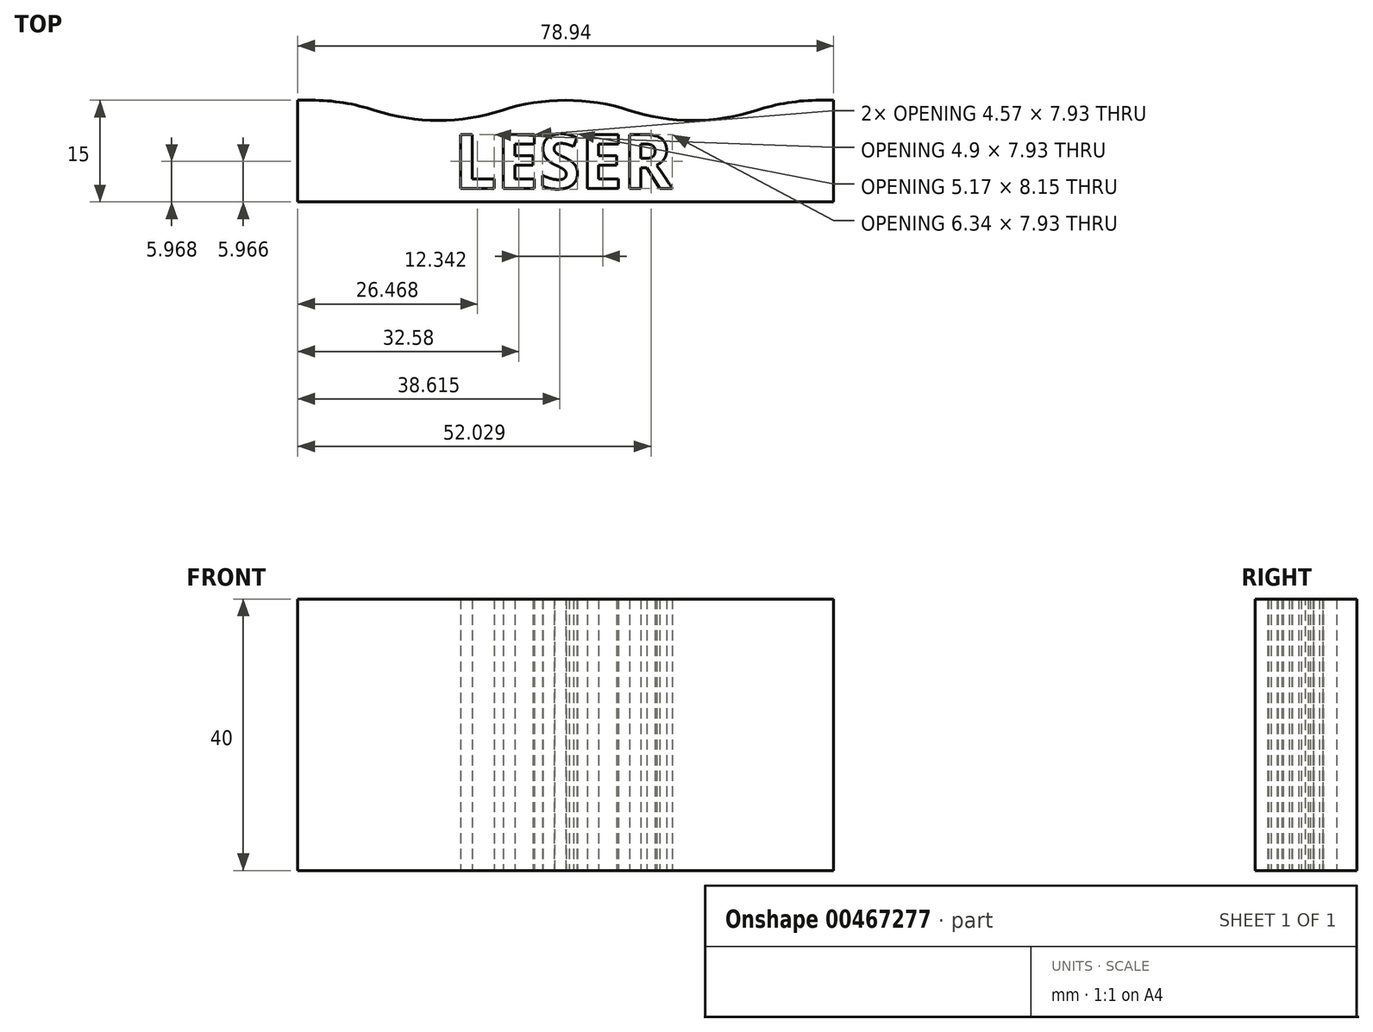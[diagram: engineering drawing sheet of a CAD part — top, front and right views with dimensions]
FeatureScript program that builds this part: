
annotation { "Feature Type Name" : "Feature", "Feature Type Description" : "" }
export const myFeature = defineFeature(function(context is Context, id is Id, definition is map)
    precondition{}
    {
        {
            var Q0;
            Q0=qCreatedBy(makeId("Top.planeOp"),FACE);
            var sketch = newSketch(context, id + "F0", { "sketchPlane" : qUnion([Q0])});
            skLineSegment(sketch, "E0", {"start": v(0, 0) * mm, "end": v(0, 15) * mm});
            skLineSegment(sketch, "E1", {"start": v(0, 15) * mm, "end": v(2, 15) * mm});
            skArc(sketch, "E2", {"start": v(2, 15) * mm, "mid": v(6.74, 14.62) * mm, "end": v(11.37, 13.5) * mm});
            skArc(sketch, "E3", {"start": v(11.37, 13.5) * mm, "mid": v(20.73, 12) * mm, "end": v(30.1, 13.5) * mm});
            skPoint(sketch, "E4.endSnap0", {"position": v(1, 15) * mm});
            skArc(sketch, "E5", {"start": v(30.1, 13.5) * mm, "mid": v(39.47, 15) * mm, "end": v(48.84, 13.5) * mm});
            skArc(sketch, "E6", {"start": v(48.84, 13.5) * mm, "mid": v(58.2, 12) * mm, "end": v(67.57, 13.5) * mm});
            skArc(sketch, "E7", {"start": v(67.57, 13.5) * mm, "mid": v(72.2, 14.62) * mm, "end": v(76.94, 15) * mm});
            skLineSegment(sketch, "E8", {"start": v(76.94, 15) * mm, "end": v(78.94, 15) * mm});
            skLineSegment(sketch, "E9", {"start": v(78.94, 15) * mm, "end": v(78.94, 0) * mm});
            skLineSegment(sketch, "E10", {"start": v(78.94, 0) * mm, "end": v(0, 0) * mm});
            skSolve(sketch);
        }
        {
            var Q0;
            Q0=makeQuery(id+"F0.imprint","IMPRINT",FACE,{"disambiguationData":[TD([[makeQuery(id+"F0.imprint","IMPRINT",EDGE,{"derivedFrom":sQuery(id+"F0.wireOp",EDGE,"E0")}),-1.0]])]});
            extrude(context, id + "F1", {"entities" : qUnion([Q0]), "depth" : 40 * mm});
        }
        {
            var Q0;
            Q0=qCreatedBy(makeId("Top.planeOp"),FACE);
            var sketch = newSketch(context, id + "F2", { "sketchPlane" : qUnion([Q0])});
            skText(sketch, "E11", { "text": "LESER", "fontName": "OpenSans-Bold.ttf"});
            const initialGuessF2  = {"E11": [0.02302, 0.002, 1, 0, 0.008]};
            skSetInitialGuess(sketch, initialGuessF2);
            skSolve(sketch);
        }
        {
            var Q0;
            Q0 = qSketchRegion(id + "F2", true);
            extrude(context, id + "F3", {"entities" : qUnion([Q0]), "operationType" : NewBodyOperationType.REMOVE, "depth" : 40 * mm});
        }
    });
